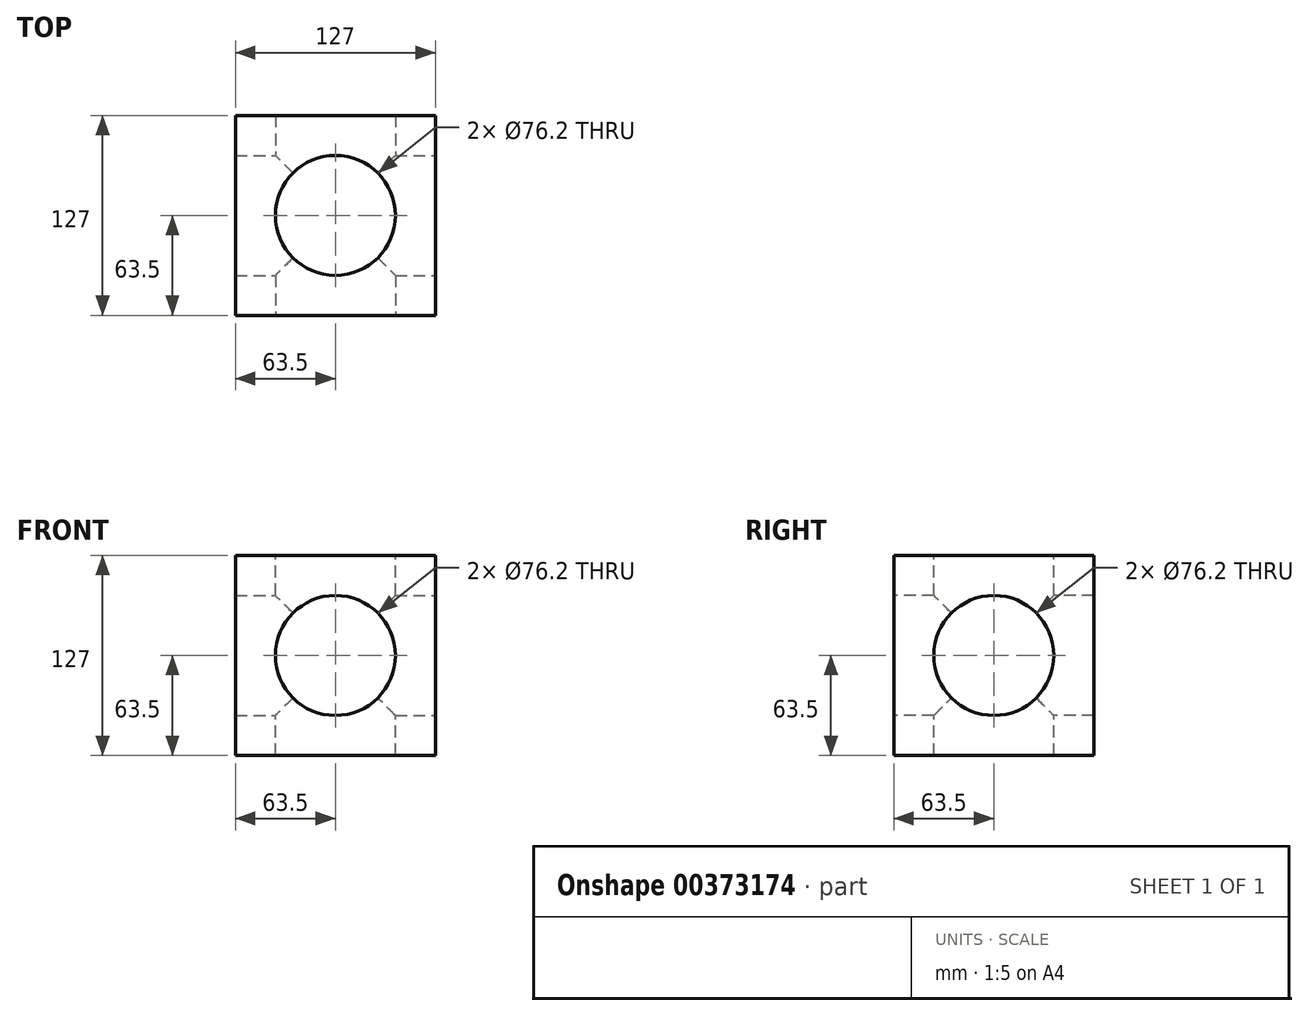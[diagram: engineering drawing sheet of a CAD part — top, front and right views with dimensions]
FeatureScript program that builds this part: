
annotation { "Feature Type Name" : "Feature", "Feature Type Description" : "" }
export const myFeature = defineFeature(function(context is Context, id is Id, definition is map)
    precondition{}
    {
        {
            var Q0;
            Q0=qCreatedBy(makeId("Top.planeOp"),FACE);
            var sketch = newSketch(context, id + "F0", { "sketchPlane" : qUnion([Q0])});
            skLineSegment(sketch, "E0.bottom", {"start": v(0, 0) * mm, "end": v(127, 0) * mm});
            skLineSegment(sketch, "E0.top", {"start": v(0, 127) * mm, "end": v(127, 127) * mm});
            skLineSegment(sketch, "E0.left", {"start": v(0, 0) * mm, "end": v(0, 127) * mm});
            skLineSegment(sketch, "E0.right", {"start": v(127, 0) * mm, "end": v(127, 127) * mm});
            skSolve(sketch);
        }
        {
            var Q0;
            Q0 = qSketchRegion(id + "F0", true);
            extrude(context, id + "F1", {"entities" : qUnion([Q0]), "depth" : 127 * mm});
        }
        {
            var Q0;
            Q0=makeQuery(id+"F1.opExtrude","SWEPT_FACE",FACE,{"disambiguationData":[OSD([sQuery(id+"F0.wireOp",EDGE,"E0.bottom")])]});
            var sketch = newSketch(context, id + "F2", { "sketchPlane" : qUnion([Q0])});
            skCircle(sketch, "E1", {"center": v(63.5, 63.5) * mm, "radius": 38.1 * mm});
            skPoint(sketch, "E1.centerSnap0", {"position": v(127, 63.5) * mm});
            skPoint(sketch, "E1.centerSnap1", {"position": v(63.5, 127) * mm});
            skSolve(sketch);
        }
        {
            var Q0;
            Q0 = qSketchRegion(id + "F2", true);
            extrude(context, id + "F3", {"entities" : qUnion([Q0]), "operationType" : NewBodyOperationType.REMOVE, "endBound" : BoundingType.THROUGH_ALL, "oppositeDirection" : true, "depth" : 25.4 * mm});
        }
        {
            var Q0;
            Q0=makeQuery(id+"F1.opExtrude","SWEPT_FACE",FACE,{"disambiguationData":[OSD([sQuery(id+"F0.wireOp",EDGE,"E0.right")])]});
            var sketch = newSketch(context, id + "F4", { "sketchPlane" : qUnion([Q0])});
            skCircle(sketch, "E2", {"center": v(63.5, 63.5) * mm, "radius": 38.1 * mm});
            skPoint(sketch, "E2.centerSnap0", {"position": v(0, 63.5) * mm});
            skPoint(sketch, "E2.centerSnap1", {"position": v(63.5, 127) * mm});
            skSolve(sketch);
        }
        {
            var Q0;
            Q0 = qSketchRegion(id + "F4", true);
            extrude(context, id + "F5", {"entities" : qUnion([Q0]), "operationType" : NewBodyOperationType.REMOVE, "endBound" : BoundingType.THROUGH_ALL, "oppositeDirection" : true, "depth" : 25.4 * mm});
        }
        {
            var Q0;
            Q0=makeQuery(id+"F1.opExtrude","CAP_FACE",FACE,{"disambiguationData":[OSD([sQuery(id+"F0.wireOp",EDGE,"E0.bottom"),sQuery(id+"F0.wireOp",EDGE,"E0.top"),sQuery(id+"F0.wireOp",EDGE,"E0.left"),sQuery(id+"F0.wireOp",EDGE,"E0.right")])],"isStart":false});
            var sketch = newSketch(context, id + "F6", { "sketchPlane" : qUnion([Q0])});
            skCircle(sketch, "E3", {"center": v(63.5, 63.5) * mm, "radius": 38.1 * mm});
            skPoint(sketch, "E3.centerSnap0", {"position": v(63.5, 0) * mm});
            skPoint(sketch, "E3.centerSnap1", {"position": v(127, 63.5) * mm});
            skSolve(sketch);
        }
        {
            var Q0;
            Q0 = qSketchRegion(id + "F6", true);
            extrude(context, id + "F7", {"entities" : qUnion([Q0]), "operationType" : NewBodyOperationType.REMOVE, "endBound" : BoundingType.THROUGH_ALL, "oppositeDirection" : true, "depth" : 25.4 * mm});
        }
    });
